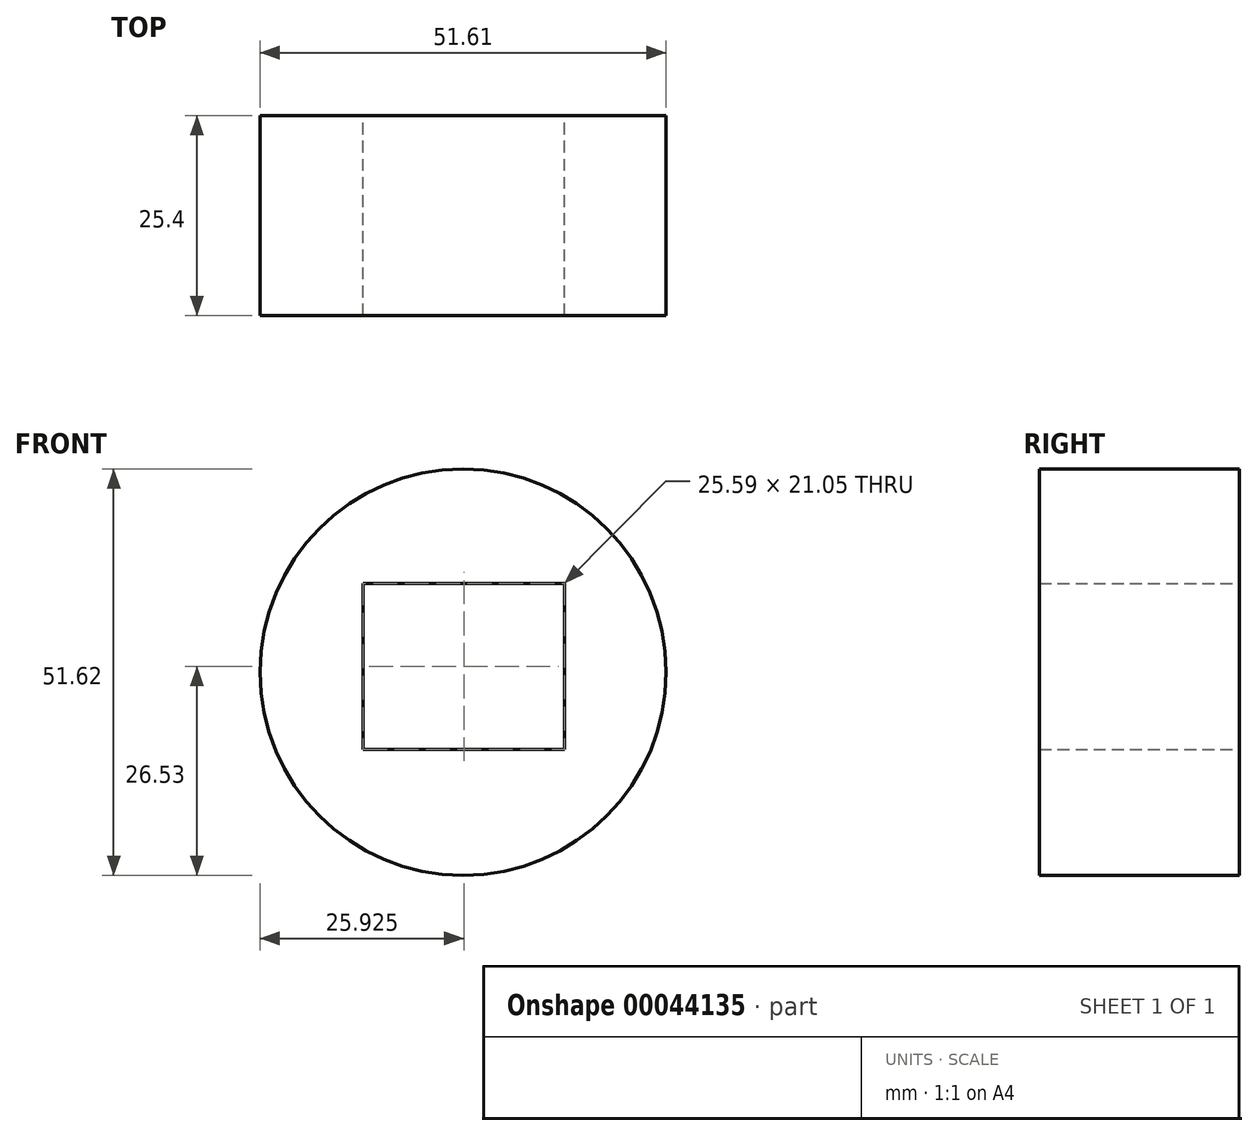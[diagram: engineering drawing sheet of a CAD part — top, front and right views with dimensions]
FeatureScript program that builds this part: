
annotation { "Feature Type Name" : "Feature", "Feature Type Description" : "" }
export const myFeature = defineFeature(function(context is Context, id is Id, definition is map)
    precondition{}
    {
        {
            var Q0;
            Q0=qCreatedBy(makeId("Front.planeOp"),FACE);
            var sketch = newSketch(context, id + "F0", { "sketchPlane" : qUnion([Q0])});
            skCircle(sketch, "E0", {"center": v(-7.65, 17.1) * mm, "radius": 25.8 * mm});
            skLineSegment(sketch, "E1.bottom", {"start": v(-20.33, 28.34) * mm, "end": v(5.26, 28.34) * mm});
            skLineSegment(sketch, "E1.top", {"start": v(-20.33, 7.3) * mm, "end": v(5.26, 7.3) * mm});
            skLineSegment(sketch, "E1.left", {"start": v(-20.33, 28.34) * mm, "end": v(-20.33, 7.3) * mm});
            skLineSegment(sketch, "E1.right", {"start": v(5.26, 28.34) * mm, "end": v(5.26, 7.3) * mm});
            skSolve(sketch);
        }
        {
            var Q0;
            Q0=makeQuery(id+"F0.imprint","IMPRINT",FACE,{"disambiguationData":[TD([[makeQuery(id+"F0.imprint","IMPRINT",EDGE,{"derivedFrom":sQuery(id+"F0.wireOp",EDGE,"E0")}),1.0]])]});
            extrude(context, id + "F1", {"entities" : qUnion([Q0]), "depth" : 25.4 * mm});
        }
    });
